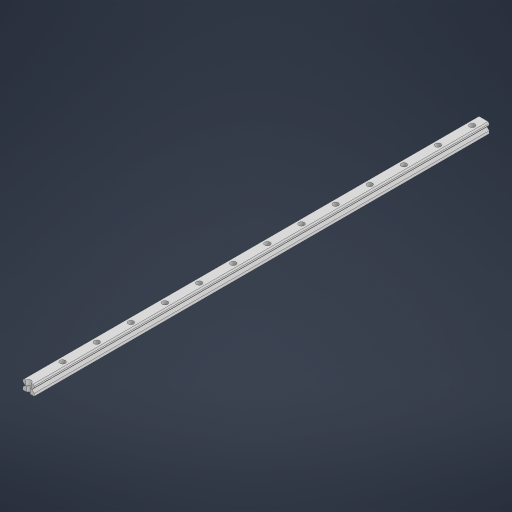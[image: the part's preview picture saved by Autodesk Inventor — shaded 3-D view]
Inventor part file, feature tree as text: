
AUTODESK INVENTOR PART (.ipt)
format: ipt  version: 2024.2 (Build 282272000, 272)  size: 240,128 bytes
history: native  units: mm
features: extrude x3, sketch x2, pattern_linear x1
ambient origin geometry x8: Origin, YZ Plane, XZ Plane, XY Plane, X Axis, Y Axis, Z Axis, Center Point
bodies: Solid1 (feature_tree)
feature tree (6):
  extrude  "Extrusion1"  Depth=20.0mm
  sketch  "Sketch2"  dims[d2=4.6mm d3=8.5mm d8=135.0deg d9=0.5mm d10=135.0deg d11=2.5mm d12=800.0mm d13=0.0mm d14=20.0mm d15=60.0mm d16=9.5mm d17=6.0mm d18=8.5mm d19=0.0mm d20=8.5mm d21=0.0mm d22=140.0mm d24=60.0mm]
  extrude  "Extrusion2"  Depth=8.5mm
  extrude  "Extrusion3"  TaperAngle=135.0deg  [1 undecoded]
  pattern_linear  "Rectangular Pattern1"  Spacing1=0.5mm  [1 undecoded]
  sketch  "Sketch1"  dims[d0=17.5mm d1=20.0mm]
note: 2 required parameter values undecoded (feature->parameter linkage not recoverable at this tier; creation-order binding heuristic only, values carry confidence <= 0.55)
